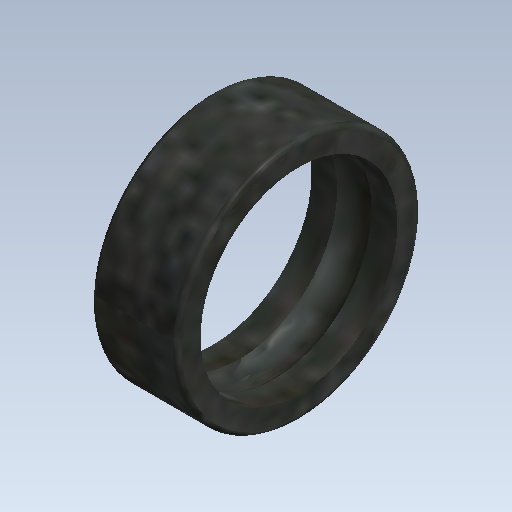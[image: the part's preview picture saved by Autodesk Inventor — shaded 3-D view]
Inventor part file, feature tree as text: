
AUTODESK INVENTOR PART (.ipt)
format: ipt  version: 2021 (Build 250183000, 183)  size: 201,216 bytes
history: native  units: mm (DEFAULTED — no unit token found)
features: other x7, revolve x1, sketch x1
ambient origin geometry x8: Origin, YZ Plane, XZ Plane, XY Plane, X Axis, Y Axis, Z Axis, Center Point
bodies: Solid1 (feature_tree)
feature tree (9):
  revolve  "Revolution1"  [1 undecoded]
  other  "ip_ot_or_XY"
  other  "ip_ot_or_YZ"
  other  "ip_ot_or_ZX"
  other  "ip_ot_or_X"
  other  "ip_ot_or_Y"
  other  "ip_ot_or_Z"
  other  "ip_ot_or_Center"
  sketch  "Sketch_1"  dims[d0=360.0deg d1=0.0mm]
note: 1 required parameter value undecoded (feature->parameter linkage not recoverable at this tier; creation-order binding heuristic only, values carry confidence <= 0.55)
